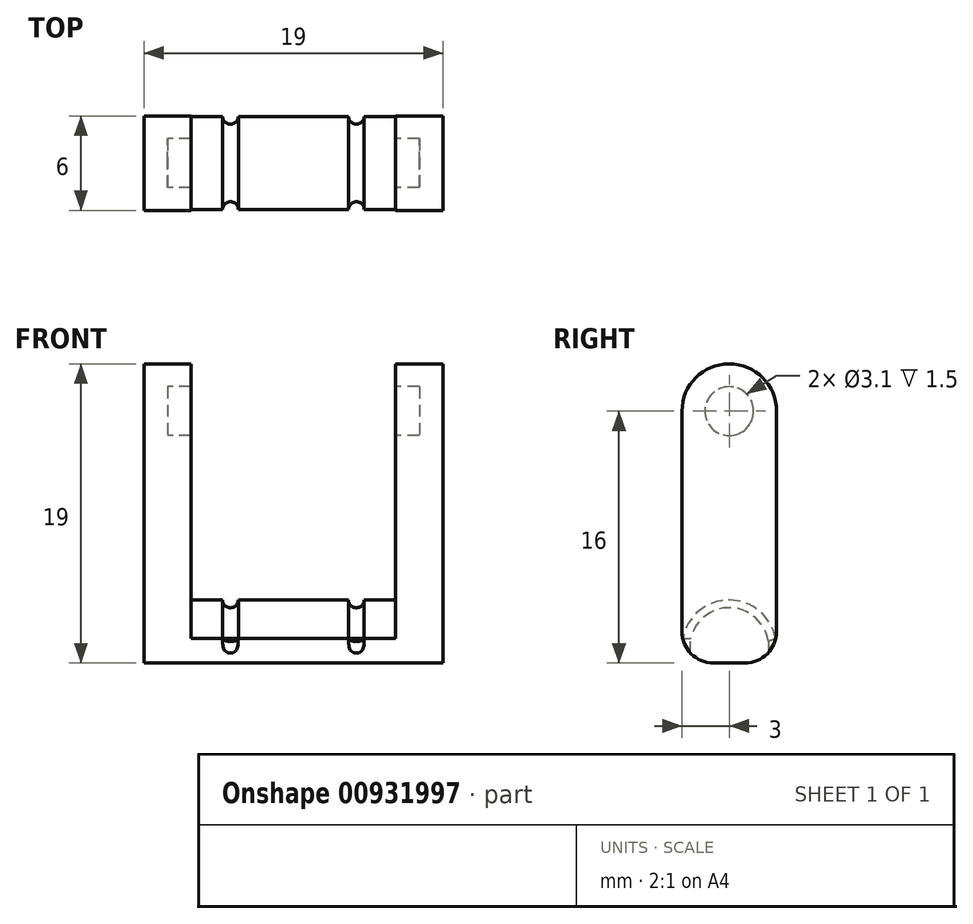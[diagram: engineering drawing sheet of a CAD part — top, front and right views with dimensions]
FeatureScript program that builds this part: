
annotation { "Feature Type Name" : "Feature", "Feature Type Description" : "" }
export const myFeature = defineFeature(function(context is Context, id is Id, definition is map)
    precondition{}
    {
        {
            var Q0;
            Q0=qCreatedBy(makeId("Front.planeOp"),FACE);
            var sketch = newSketch(context, id + "F0", { "sketchPlane" : qUnion([Q0])});
            skLineSegment(sketch, "E0", {"start": v(0, 0) * mm, "end": v(-13, 0) * mm});
            skLineSegment(sketch, "E1", {"start": v(-13, 0) * mm, "end": v(-13, 15) * mm});
            skLineSegment(sketch, "E2", {"start": v(-13, 15) * mm, "end": v(-16, 15) * mm});
            skLineSegment(sketch, "E3", {"start": v(-16, 15) * mm, "end": v(-16, -4) * mm});
            skLineSegment(sketch, "E4", {"start": v(-16, -4) * mm, "end": v(3, -4) * mm});
            skLineSegment(sketch, "E5", {"start": v(3, -4) * mm, "end": v(3, 15) * mm});
            skLineSegment(sketch, "E6", {"start": v(3, 15) * mm, "end": v(0, 15) * mm});
            skLineSegment(sketch, "E7", {"start": v(0, 15) * mm, "end": v(0, 0) * mm});
            skSolve(sketch);
        }
        {
            var Q0;
            Q0=makeQuery(id+"F0.imprint","IMPRINT",FACE,{"disambiguationData":[TD([[makeQuery(id+"F0.imprint","IMPRINT",EDGE,{"derivedFrom":sQuery(id+"F0.wireOp",EDGE,"E0")}),1.0]])]});
            extrude(context, id + "F1", {"entities" : qUnion([Q0]), "depth" : 6 * mm, "offsetDistance" : 25 * mm});
        }
        {
            var Q0;
            Q0=makeQuery(id+"F1.opExtrude","CAP_EDGE",EDGE,{"disambiguationData":[OSD([sQuery(id+"F0.wireOp",EDGE,"E4")])],"isStart":false});
            var Q1;
            Q1=makeQuery(id+"F1.opExtrude","CAP_EDGE",EDGE,{"disambiguationData":[OSD([sQuery(id+"F0.wireOp",EDGE,"E4")])],"isStart":true});
            fillet(context, id + "F2", {"entities" : qUnion([Q0, Q1]), "radius" : 2 * mm, "tangentPropagation" : true, "allowEdgeOverflow" : false});
        }
        {
            var Q0;
            Q0=makeQuery(id+"F1.opExtrude","CAP_EDGE",EDGE,{"disambiguationData":[OSD([sQuery(id+"F0.wireOp",EDGE,"E0")])],"isStart":false});
            var Q1;
            Q1=makeQuery(id+"F1.opExtrude","CAP_EDGE",EDGE,{"disambiguationData":[OSD([sQuery(id+"F0.wireOp",EDGE,"E0")])],"isStart":true});
            fillet(context, id + "F3", {"entities" : qUnion([Q0, Q1]), "radius" : 3 * mm, "tangentPropagation" : true, "allowEdgeOverflow" : false});
        }
        {
            var Q0;
            {var subQ0=sQuery(id+"F0.wireOp",EDGE,"E4");Q0=makeQuery(id+"F3.opFillet","BLEND_EDGE",EDGE,{"blendedFrom":[makeQuery(id+"F1.opExtrude","CAP_EDGE",EDGE,{"disambiguationData":[OSD([sQuery(id+"F0.wireOp",EDGE,"E0")])],"isStart":false}),makeQuery(id+"F2.opFillet","BLEND_FACE",FACE,{"disambiguationData":[OSD([subQ0]),TDD([makeQuery(id+"F1.opExtrude","CAP_EDGE",EDGE,{"disambiguationData":[OSD([subQ0])],"isStart":false})])]})],"blendedInto":[makeQuery(id+"F2.opFillet","BLEND_FACE",FACE,{"disambiguationData":[OSD([subQ0]),TDD([makeQuery(id+"F1.opExtrude","CAP_EDGE",EDGE,{"disambiguationData":[OSD([subQ0])],"isStart":false})])]})]});}
            cPlane(context, id + "F4", {"entities" : qUnion([Q0]), "cplaneType" : CPlaneType.LINE_ANGLE, "offset" : 25 * mm, "angle" : 90 * degree, "width" : 150 * mm, "height" : 150 * mm});
        }
        {
            var Q0;
            Q0=qCreatedBy(id+"F4.planeOp",FACE);
            var sketch = newSketch(context, id + "F5", { "sketchPlane" : qUnion([Q0])});
            skCircle(sketch, "E8", {"center": v(-10.5, -5.95) * mm, "radius": 0.5 * mm});
            skLineSegment(sketch, "E9", {"start": v(-13, -5.95) * mm, "end": v(-10.5, -5.95) * mm, "construction": true});
            skLineSegment(sketch, "E10", {"start": v(0, -5.95) * mm, "end": v(-2.5, -5.95) * mm, "construction": true});
            skCircle(sketch, "E11", {"center": v(-2.5, -5.95) * mm, "radius": 0.5 * mm});
            skSolve(sketch);
        }
        {
            var Q0;
            Q0=makeQuery(id+"F5.imprint","IMPRINT",FACE,{"disambiguationData":[TD([[makeQuery(id+"F5.imprint","IMPRINT",EDGE,{"derivedFrom":sQuery(id+"F5.wireOp",EDGE,"E8")}),1.0]])]});
            var Q1;
            Q1=makeQuery(id+"F5.imprint","IMPRINT",FACE,{"disambiguationData":[TD([[makeQuery(id+"F5.imprint","IMPRINT",EDGE,{"derivedFrom":sQuery(id+"F5.wireOp",EDGE,"E11")}),1.0]])]});
            var Q2;
            Q2=sQuery(id+"F5.wireOp",EDGE,"E8");
            var Q3;
            Q3=makeQuery(id+"F3.opFillet","BLEND_EDGE",EDGE,{"blendedFrom":[makeQuery(id+"F1.opExtrude","CAP_EDGE",EDGE,{"disambiguationData":[OSD([sQuery(id+"F0.wireOp",EDGE,"E0")])],"isStart":true}),makeQuery(id+"F1.opExtrude","SWEPT_FACE",FACE,{"disambiguationData":[OSD([sQuery(id+"F0.wireOp",EDGE,"E1")])]})],"blendedInto":[makeQuery(id+"F1.opExtrude","SWEPT_FACE",FACE,{"disambiguationData":[OSD([sQuery(id+"F0.wireOp",EDGE,"E1")])]})]});
            sweep(context, id + "F6", {"operationType" : NewBodyOperationType.REMOVE, "profiles" : qUnion([Q0, Q1]), "surfaceProfiles" : qUnion([Q2]), "path" : qUnion([Q3])});
        }
        {
            var Q0;
            Q0=makeQuery(id+"F6.boolean.opBoolean","COPY",FACE,{"derivedFrom":makeQuery(id+"F6.opSweep","CAP_FACE",FACE,{"disambiguationData":[OSD([sQuery(id+"F0.wireOp",EDGE,"E0"),sQuery(id+"F0.wireOp",EDGE,"E1"),sQuery(id+"F0.wireOp",EDGE,"E4"),sQuery(id+"F5.wireOp",EDGE,"E8")])],"isStart":true})});
            var Q1;
            Q1=makeQuery(id+"F6.boolean.opBoolean","COPY",FACE,{"derivedFrom":makeQuery(id+"F6.opSweep","CAP_FACE",FACE,{"disambiguationData":[OSD([sQuery(id+"F0.wireOp",EDGE,"E0"),sQuery(id+"F0.wireOp",EDGE,"E1"),sQuery(id+"F0.wireOp",EDGE,"E4"),sQuery(id+"F5.wireOp",EDGE,"E11")])],"isStart":true})});
            var Q2;
            Q2=makeQuery(id+"F6.boolean.opBoolean","COPY",FACE,{"derivedFrom":makeQuery(id+"F6.opSweep","CAP_FACE",FACE,{"disambiguationData":[OSD([sQuery(id+"F0.wireOp",EDGE,"E0"),sQuery(id+"F0.wireOp",EDGE,"E1"),sQuery(id+"F0.wireOp",EDGE,"E4"),sQuery(id+"F5.wireOp",EDGE,"E11")])],"isStart":false})});
            var Q3;
            Q3=makeQuery(id+"F6.boolean.opBoolean","COPY",FACE,{"derivedFrom":makeQuery(id+"F6.opSweep","CAP_FACE",FACE,{"disambiguationData":[OSD([sQuery(id+"F0.wireOp",EDGE,"E0"),sQuery(id+"F0.wireOp",EDGE,"E1"),sQuery(id+"F0.wireOp",EDGE,"E4"),sQuery(id+"F5.wireOp",EDGE,"E8")])],"isStart":false})});
            extrude(context, id + "F7", {"entities" : qUnion([Q0, Q1, Q2, Q3]), "operationType" : NewBodyOperationType.REMOVE, "oppositeDirection" : true, "depth" : 25 * mm, "offsetDistance" : 25 * mm});
        }
        {
            var Q0;
            Q0=makeQuery(id+"F1.opExtrude","SWEPT_FACE",FACE,{"disambiguationData":[OSD([sQuery(id+"F0.wireOp",EDGE,"E7")])]});
            var sketch = newSketch(context, id + "F8", { "sketchPlane" : qUnion([Q0])});
            skLineSegment(sketch, "E12", {"start": v(3, 15) * mm, "end": v(3, 12) * mm, "construction": true});
            skLineSegment(sketch, "E13", {"start": v(3, 12) * mm, "end": v(0, 12) * mm, "construction": true});
            skCircle(sketch, "E14", {"center": v(3, 12) * mm, "radius": 1.55 * mm});
            skSolve(sketch);
        }
        {
            var Q0;
            Q0 = qSketchRegion(id + "F8", true);
            extrude(context, id + "F9", {"entities" : qUnion([Q0]), "operationType" : NewBodyOperationType.REMOVE, "oppositeDirection" : true, "depth" : 1.5 * mm, "offsetDistance" : 25 * mm, "hasSecondDirection" : true, "secondDirectionOppositeDirection" : false, "secondDirectionDepth" : 14.5 * mm});
        }
        {
            var Q0;
            Q0=makeQuery(id+"F1.opExtrude","CAP_EDGE",EDGE,{"disambiguationData":[OSD([sQuery(id+"F0.wireOp",EDGE,"E2")])],"isStart":false});
            var Q1;
            Q1=makeQuery(id+"F1.opExtrude","CAP_EDGE",EDGE,{"disambiguationData":[OSD([sQuery(id+"F0.wireOp",EDGE,"E2")])],"isStart":true});
            var Q2;
            Q2=makeQuery(id+"F1.opExtrude","CAP_EDGE",EDGE,{"disambiguationData":[OSD([sQuery(id+"F0.wireOp",EDGE,"E6")])],"isStart":true});
            var Q3;
            Q3=makeQuery(id+"F1.opExtrude","CAP_EDGE",EDGE,{"disambiguationData":[OSD([sQuery(id+"F0.wireOp",EDGE,"E6")])],"isStart":false});
            fillet(context, id + "F10", {"entities" : qUnion([Q0, Q1, Q2, Q3]), "radius" : 3 * mm, "tangentPropagation" : true, "allowEdgeOverflow" : false});
        }
    });
